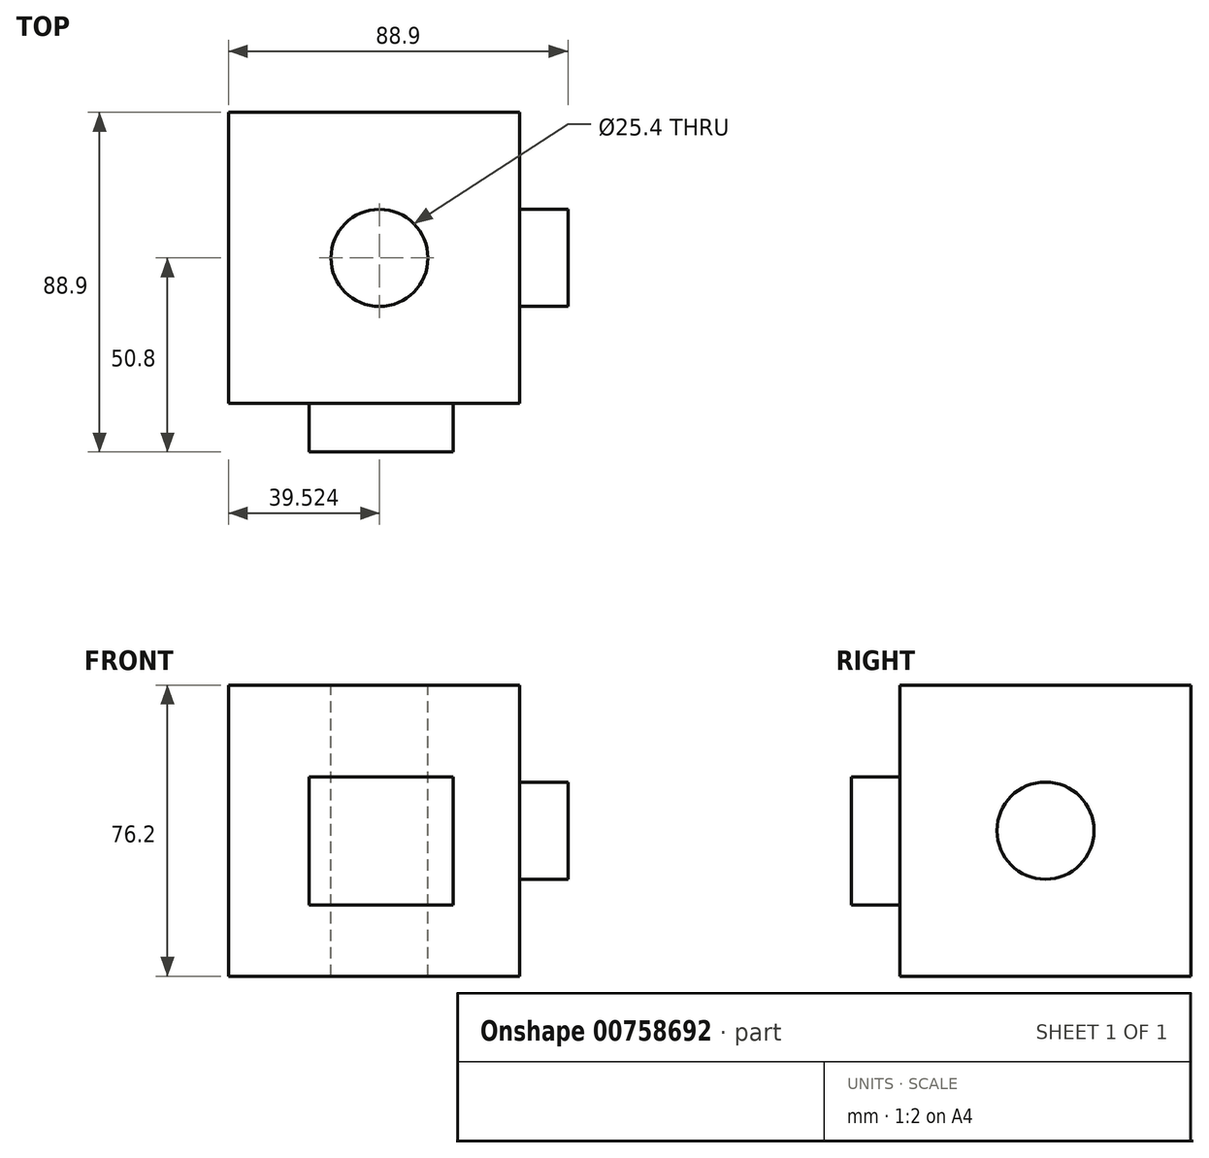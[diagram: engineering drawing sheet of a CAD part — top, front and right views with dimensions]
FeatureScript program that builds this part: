
annotation { "Feature Type Name" : "Feature", "Feature Type Description" : "" }
export const myFeature = defineFeature(function(context is Context, id is Id, definition is map)
    precondition{}
    {
        {
            var Q0;
            Q0=qCreatedBy(makeId("Front.planeOp"),FACE);
            var sketch = newSketch(context, id + "F0", { "sketchPlane" : qUnion([Q0])});
            skLineSegment(sketch, "E0.bottom", {"start": v(-47.51, 60.4) * mm, "end": v(28.69, 60.4) * mm});
            skLineSegment(sketch, "E0.top", {"start": v(-47.51, -15.8) * mm, "end": v(28.69, -15.8) * mm});
            skLineSegment(sketch, "E0.left", {"start": v(-47.51, 60.4) * mm, "end": v(-47.51, -15.8) * mm});
            skLineSegment(sketch, "E0.right", {"start": v(28.69, 60.4) * mm, "end": v(28.69, -15.8) * mm});
            skSolve(sketch);
        }
        {
            var Q0;
            Q0=makeQuery(id+"F0.imprint","IMPRINT",FACE,{"disambiguationData":[TD([[makeQuery(id+"F0.imprint","IMPRINT",EDGE,{"derivedFrom":sQuery(id+"F0.wireOp",EDGE,"E0.bottom")}),-1.0]])]});
            extrude(context, id + "F1", {"entities" : qUnion([Q0]), "depth" : 76.2 * mm, "offsetDistance" : 25.4 * mm});
        }
        {
            var Q0;
            Q0=makeQuery(id+"F1.opExtrude","CAP_FACE",FACE,{"disambiguationData":[OSD([sQuery(id+"F0.wireOp",EDGE,"E0.bottom"),sQuery(id+"F0.wireOp",EDGE,"E0.top"),sQuery(id+"F0.wireOp",EDGE,"E0.left"),sQuery(id+"F0.wireOp",EDGE,"E0.right")])],"isStart":false});
            var sketch = newSketch(context, id + "F2", { "sketchPlane" : qUnion([Q0])});
            skLineSegment(sketch, "E1.bottom", {"start": v(-26.37, 36.42) * mm, "end": v(11.27, 36.42) * mm});
            skLineSegment(sketch, "E1.top", {"start": v(-26.37, 2.86) * mm, "end": v(11.27, 2.86) * mm});
            skLineSegment(sketch, "E1.left", {"start": v(-26.37, 36.42) * mm, "end": v(-26.37, 2.86) * mm});
            skLineSegment(sketch, "E1.right", {"start": v(11.27, 36.42) * mm, "end": v(11.27, 2.86) * mm});
            skSolve(sketch);
        }
        {
            var Q0;
            Q0 = qSketchRegion(id + "F2", true);
            extrude(context, id + "F3", {"entities" : qUnion([Q0]), "operationType" : NewBodyOperationType.ADD, "depth" : 12.7 * mm, "offsetDistance" : 25.4 * mm});
        }
        {
            var Q0;
            Q0=makeQuery(id+"F1.opExtrude","SWEPT_FACE",FACE,{"disambiguationData":[OSD([sQuery(id+"F0.wireOp",EDGE,"E0.right")])]});
            var sketch = newSketch(context, id + "F4", { "sketchPlane" : qUnion([Q0])});
            skCircle(sketch, "E2", {"center": v(-38.1, 22.3) * mm, "radius": 12.7 * mm});
            skSolve(sketch);
        }
        {
            var Q0;
            Q0=makeQuery(id+"F4.imprint","IMPRINT",FACE,{"disambiguationData":[TD([[makeQuery(id+"F4.imprint","IMPRINT",EDGE,{"derivedFrom":sQuery(id+"F4.wireOp",EDGE,"E2")}),1.0]])]});
            extrude(context, id + "F5", {"entities" : qUnion([Q0]), "operationType" : NewBodyOperationType.ADD, "depth" : 12.7 * mm, "offsetDistance" : 25.4 * mm});
        }
        {
            var Q0;
            Q0=makeQuery(id+"F1.opExtrude","SWEPT_FACE",FACE,{"disambiguationData":[OSD([sQuery(id+"F0.wireOp",EDGE,"E0.bottom")])]});
            var sketch = newSketch(context, id + "F6", { "sketchPlane" : qUnion([Q0])});
            skPoint(sketch, "E3", {"position": v(-7.99, -38.1) * mm});
            skSolve(sketch);
        }
        {
            var Q0;
            Q0=sQuery(id+"F6.wireOp",VERTEX,"E3");
            var Q1;
            Q1=makeQuery(id+"F1.opExtrude","SWEPT_BODY",BODY,{"disambiguationData":[OSD([sQuery(id+"F0.wireOp",EDGE,"E0.bottom"),sQuery(id+"F0.wireOp",EDGE,"E0.top"),sQuery(id+"F0.wireOp",EDGE,"E0.left"),sQuery(id+"F0.wireOp",EDGE,"E0.right")])]});
            hole(context, id + "F7", {"style" : HoleStyle.SIMPLE, "endStyle" : HoleEndStyle.THROUGH, "holeDiameter" : 25.4 * mm, "majorDiameter" : 6.35 * mm, "isTappedThrough" : true, "tappedDepth" : 12.7 * mm, "tapClearance" : 3, "locations" : qUnion([Q0]), "scope" : qUnion([Q1])});
        }
    });
